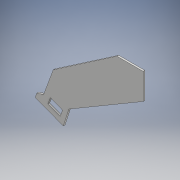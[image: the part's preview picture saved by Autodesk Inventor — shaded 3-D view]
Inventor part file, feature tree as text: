
AUTODESK INVENTOR PART (.ipt)
format: ipt  version: 2018 (Build 220112000, 112)  size: 116,224 bytes
history: native  units: mm
features: extrude x2, sketch x2
ambient origin geometry x8: Origin, YZ Plane, XZ Plane, XY Plane, X Axis, Y Axis, Z Axis, Center Point
bodies: Solide1 (feature_tree)
feature tree (4):
  extrude  "Extrusion1"  Depth=45.0mm
  extrude  "Extrusion2"  Depth=45.0mm
  sketch  "Esquisse1"
  sketch  "Esquisse2"
